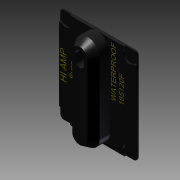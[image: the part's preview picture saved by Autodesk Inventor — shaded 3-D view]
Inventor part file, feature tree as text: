
AUTODESK INVENTOR PART (.ipt)
format: ipt  version: 2011 (Build 150239000, 239)  size: 641,536 bytes
history: native  units: mm (DEFAULTED — no unit token found)
features: sketch x6, extrude x4, plane x2, mirror x2, emboss x2, chamfer x1, reference x1
ambient origin geometry x8: Origin, YZ Plane, XZ Plane, XY Plane, X Axis, Y Axis, Z Axis, Center Point
bodies: Solid1 (feature_tree)
feature tree (18):
  extrude  "Extrusion1"  Depth=6.35mm
  extrude  "Extrusion2"  Depth=3.81mm
  chamfer  "Chamfer2"  Distance=8.89mm
  extrude  "Extrusion3"  Depth=0.762mm
  plane  "Work Plane1"
  plane  "Work Plane2"
  extrude  "Extrusion5"  Depth=0.762mm TaperAngle=0.0deg
  mirror  "Mirror3"
  mirror  "Mirror4"
  emboss  "Emboss1"
  emboss  "Emboss2"
  sketch  "Sketch1"  dims[d0=1.524mm d1=0.0mm d2=6.35mm]
  reference  "Reference1"
  sketch  "Sketch2"  dims[d3=8.89mm d4=0.0mm d7=3.81mm d8=2.54mm]
  sketch  "Sketch3"  dims[d10=2.159mm]
  sketch  "Sketch5"  dims[d11=7.62mm d12=8.89mm d13=0.0mm]
  sketch  "Sketch6"  dims[d17=6.35mm d18=0.762mm]
  sketch  "Sketch7"  dims[d19=0.762mm d20=0.762mm d21=0.0mm d22=0.0508mm d23=0.0mm d24=0.0508mm d25=0.0mm d26=45.0deg]
